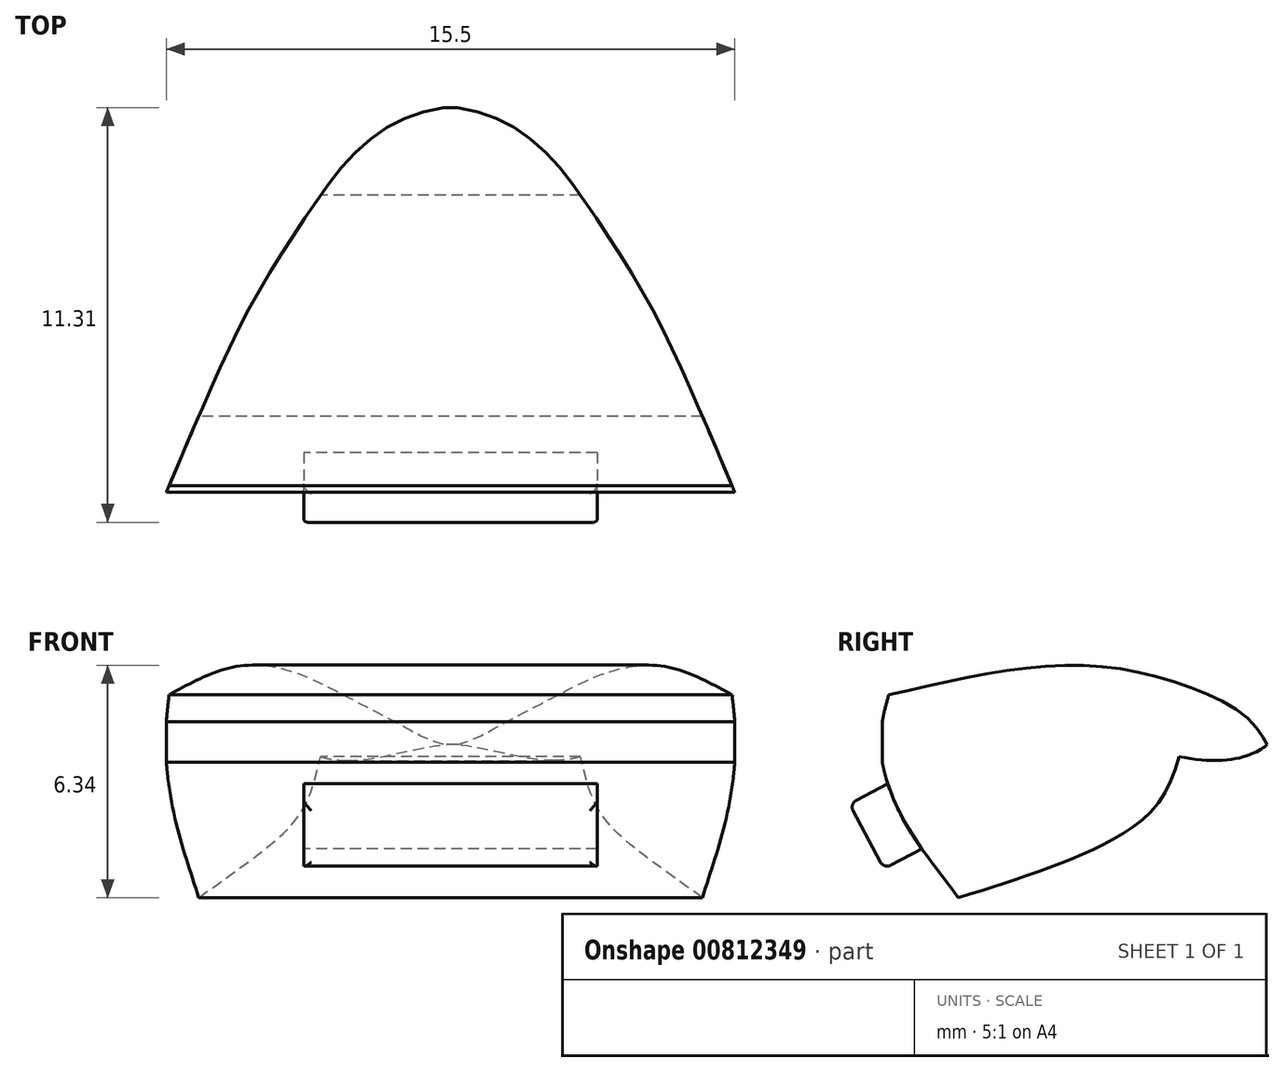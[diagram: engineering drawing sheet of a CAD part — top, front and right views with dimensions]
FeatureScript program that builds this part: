
annotation { "Feature Type Name" : "Feature", "Feature Type Description" : "" }
export const myFeature = defineFeature(function(context is Context, id is Id, definition is map)
    precondition{}
    {
        {
            var Q0;
            Q0=qCreatedBy(makeId("Right.planeOp"),FACE);
            var sketch = newSketch(context, id + "F0", { "sketchPlane" : qUnion([Q0])});
            skPoint(sketch, "E0", {"position": v(40.6, 0) * mm});
            skPoint(sketch, "E1", {"position": v(0, -40.6) * mm});
            skSolve(sketch);
        }
        {
            var Q0;
            Q0=qCreatedBy(makeId("Right.planeOp"),FACE);
            var sketch = newSketch(context, id + "F1", { "sketchPlane" : qUnion([Q0])});
            skFitSpline(sketch, "E2", {"points": [v(15.98, 20.34) * mm, v(19.6, 21.06) * mm, v(22.75, 20.97) * mm, v(25.64, 19.81) * mm, v(26.3, 18.99) * mm], "startDerivative": vector(12.45, 2.9) * mm, "endDerivative": vector(2.67, -5.07) * mm});
            skFitSpline(sketch, "E3", {"points": [v(26.3, 18.99) * mm, v(25.27, 18.58) * mm, v(23.9, 18.66) * mm], "startDerivative": vector(-1.52, -1.52) * mm, "endDerivative": vector(-3.1, 0.67) * mm});
            skFitSpline(sketch, "E4", {"points": [v(23.9, 18.66) * mm, v(23.26, 17.3) * mm, v(21.3, 16.01) * mm, v(17.87, 14.8) * mm], "startDerivative": vector(-1.72, -5.4) * mm, "endDerivative": vector(-8.82, -2.75) * mm});
            skFitSpline(sketch, "E5", {"points": [v(17.87, 14.8) * mm, v(16.43, 16.84) * mm, v(15.76, 18.78) * mm, v(15.98, 20.34) * mm], "startDerivative": vector(-5.38, 7.64) * mm, "endDerivative": vector(1.52, 5.49) * mm});
            skFitSpline(sketch, "E6", {"points": [v(15.9, 18.06) * mm, v(17.54, 18.67) * mm, v(20.82, 19.38) * mm, v(22.57, 19.1) * mm, v(23.9, 18.66) * mm], "startDerivative": vector(6.28, 2.5) * mm, "endDerivative": vector(6.3, -2.18) * mm});
            skSolve(sketch);
        }
        {
            var Q0;
            Q0 = qSketchRegion(id + "F1", true);
            extrude(context, id + "F2", {"entities" : qUnion([Q0]), "depth" : 15.5 * mm, "offsetDistance" : 25 * mm, "symmetric" : true});
        }
        {
            var Q0;
            Q0=qCreatedBy(makeId("Top.planeOp"),FACE);
            var sketch = newSketch(context, id + "F3", { "sketchPlane" : qUnion([Q0])});
            skLineSegment(sketch, "E7", {"start": v(-7.75, 15.8) * mm, "end": v(7.75, 15.8) * mm});
            skFitSpline(sketch, "E8", {"points": [v(-7.75, 15.8) * mm, v(-5.72, 20.36) * mm, v(-3.9, 23.4) * mm, v(0, 26.31) * mm], "startDerivative": vector(3.94, 9.2) * mm, "endDerivative": vector(17.91, 1.61) * mm});
            skFitSpline(sketch, "E9.MirrorCS", {"points": [v(7.75, 15.8) * mm, v(5.72, 20.36) * mm, v(3.9, 23.4) * mm, v(0, 26.31) * mm], "startDerivative": vector(-3.94, 9.2) * mm, "endDerivative": vector(-17.91, 1.61) * mm});
            skSolve(sketch);
        }
        {
            var Q0;
            Q0 = qSketchRegion(id + "F3", true);
            extrude(context, id + "F4", {"entities" : qUnion([Q0]), "operationType" : NewBodyOperationType.INTERSECT, "depth" : 25 * mm, "offsetDistance" : 25 * mm});
        }
        {
            var Q0;
            Q0=qCreatedBy(makeId("Right.planeOp"),FACE);
            var sketch = newSketch(context, id + "F5", { "sketchPlane" : qUnion([Q0])});
            skLineSegment(sketch, "E10", {"start": v(14.91, 17.37) * mm, "end": v(16.24, 18.07) * mm});
            skLineSegment(sketch, "E11", {"start": v(16.24, 18.07) * mm, "end": v(17.17, 16.3) * mm});
            skLineSegment(sketch, "E12", {"start": v(17.17, 16.3) * mm, "end": v(15.85, 15.6) * mm});
            skLineSegment(sketch, "E13", {"start": v(14.91, 17.37) * mm, "end": v(15.85, 15.6) * mm});
            skSolve(sketch);
        }
        {
            var Q0;
            Q0=makeQuery(id+"F5.imprint","IMPRINT",FACE,{"disambiguationData":[TD([[makeQuery(id+"F5.imprint","IMPRINT",EDGE,{"derivedFrom":sQuery(id+"F5.wireOp",EDGE,"E10")}),-1.0]])]});
            extrude(context, id + "F6", {"entities" : qUnion([Q0]), "operationType" : NewBodyOperationType.ADD, "depth" : 8 * mm, "offsetDistance" : 25 * mm, "symmetric" : true});
        }
        {
            var Q0;
            Q0=makeQuery(id+"F6.opExtrude","CAP_EDGE",EDGE,{"disambiguationData":[OSD([sQuery(id+"F5.wireOp",EDGE,"E13")])],"isStart":false});
            var Q1;
            Q1=makeQuery(id+"F6.opExtrude","SWEPT_EDGE",EDGE,{"disambiguationData":[OSD([sQuery(id+"F5.wireOp",EDGE,"E10"),sQuery(id+"F5.wireOp",EDGE,"E13")])]});
            var Q2;
            Q2=makeQuery(id+"F6.opExtrude","CAP_EDGE",EDGE,{"disambiguationData":[OSD([sQuery(id+"F5.wireOp",EDGE,"E13")])],"isStart":true});
            var Q3;
            Q3=makeQuery(id+"F6.opExtrude","SWEPT_EDGE",EDGE,{"disambiguationData":[OSD([sQuery(id+"F5.wireOp",EDGE,"E12"),sQuery(id+"F5.wireOp",EDGE,"E13")])]});
            fillet(context, id + "F7", {"entities" : qUnion([Q0, Q1, Q2, Q3]), "radius" : .2 * mm, "tangentPropagation" : true, "allowEdgeOverflow" : false});
        }
    });
